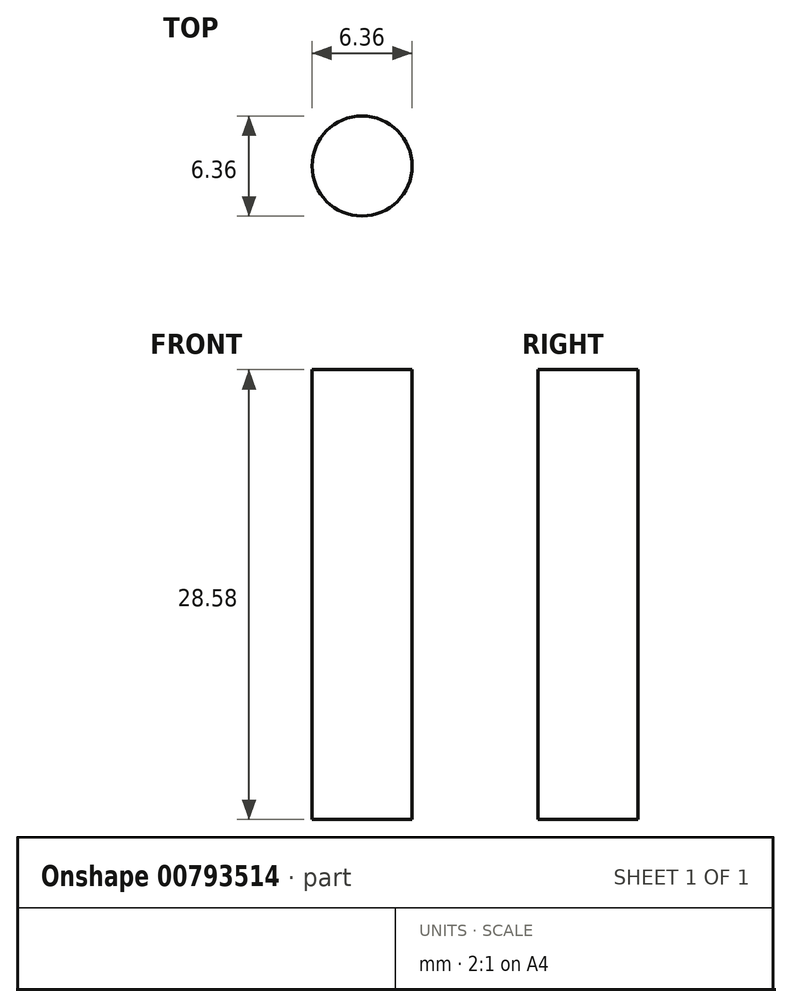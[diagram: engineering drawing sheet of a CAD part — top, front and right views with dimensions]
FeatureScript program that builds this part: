
annotation { "Feature Type Name" : "Feature", "Feature Type Description" : "" }
export const myFeature = defineFeature(function(context is Context, id is Id, definition is map)
    precondition{}
    {
        {
            var Q0;
            Q0=qCreatedBy(makeId("Top.planeOp"),FACE);
            var sketch = newSketch(context, id + "F0", { "sketchPlane" : qUnion([Q0])});
            skCircle(sketch, "E0", {"center": v(0, 0) * mm, "radius": 3.18 * mm});
            skSolve(sketch);
        }
        {
            var Q0;
            Q0=qSketchRegion(id+"F0",true);
            extrude(context, id + "F1", {"entities" : qUnion([Q0]), "depth" : 28.57 * mm, "offsetDistance" : 25.4 * mm});
        }
    });
